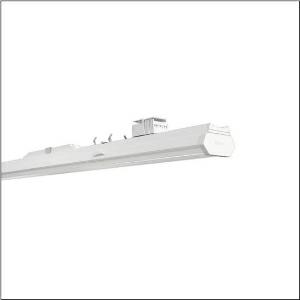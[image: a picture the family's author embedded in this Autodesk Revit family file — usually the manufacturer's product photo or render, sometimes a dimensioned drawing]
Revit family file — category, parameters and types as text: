
# Revit family: licross_r__11_protected_mo_51td1bdn49xg3s4_3b80
name_source: partatom
category: Lighting Fixtures
units: mm (PartAtom-declared; Revit-internal decimal feet)

## family parameters
Cut with Voids When Loaded = No
Host = Face
Light Source = No
Part Type = Normal
Room Calculation Point = No
Round Connector Dimension = Use Diameter
Shared = No

## types (1)
- --- (1 x LED, 920 lm, 6.8 W, 4000K)
    Apparent Load = 7 VA
    CIE Flux Codes = 54 82 95 97 100
    Color Rendering = 80
    Color Temperature = 4000K
    Default Elevation = 1800 mm
    Description = Licross® 11 Protected MO, luminaire insert, of sheet steel, galvanised, coil coated, white, length: 1.500mm, width: 90mm, height: 101mm, LED rated luminous flux: 9.370lm, light colour: 840, control gear: DALI 2, with plug, 6-pole, with phase selection, for trunking rail, 9 or 11-core, mains connection: 220..240V, AC, 50/60Hz, rated input power: 61W, for trunking rail, 9-/11-core, halogen-free wiring, for emergency light function, converter,control gear: single battery element, battery: LiFePO4, 9Ah, primary optical cover: cover, of PMMA, light emission: direct distribution, primary light characteristic: symmetric, protection rating (complete): IP54, insulation class (complete): insulation class I (protective earthing), certification: CE, UKCA, protection symbol: D if used in an environment with non-conductive dust loads with corresponding accessories, impact resistance: IK06, permissible ambient temperature for indoor applications: +5..+35°C, standard: EN 60598-2-22, LABS conformity tested according to VDMA 24364:2018-05, reducing of maximum allowable ambient temperature of 5°C with ceiling mounting, corresponds to IFS (International Featured Standards) requirements for safety and quality in the food industry, packaging unit: 1 piece
    Height = 92 mm
    Lamp = 1 x LED
    Lamp Light Flux = 920 lm
    Lamp Power = 6.8 W
    Lamp count = 1
    Length = 1500 mm
    Luminous efficacy = 135 lm/W
    Manufacturer = Siteco
    ModVariant = No
    Model = 51TD1BDN49XG3S4
    Mounting Place = Ceiling
    Mounting Type = Pendant
    Number of Poles = 1
    OnlyDefault = Yes
    Power Factor = 1
    Product Name = Licross® 11 Protected MO
    Product group = luminaire insert
    ProductGroupID = 902
    Protection Class = Protection class I
    Protection Degree = IP 54
    RLX_Detail_Level = 1
    RLX_Emergency_Light_Flux = 0 lm
    RLX_Emergency_Type = 0
    RLX_Emergency_Type_DB = No
    RlxData = <blob elided: 24661 chars, md5=6ff04b1c>
    Socket = socket
    Standby Power = 0 W
    System Light Flux = 920 lm
    System Power = 7 W
    Type Comments = : emergency light operation: 3 h
    Type Image = l_1256145.jpg
    URL = http://relux.com
    VarID = @adj_091036
    Voltage = 0 V
    Weight = 0.00 kg
    Width = 88 mm

## geometry (parser evidence)
native form markers: Blend x4, Sweep x11
no freeform markers — native parametric forms only
